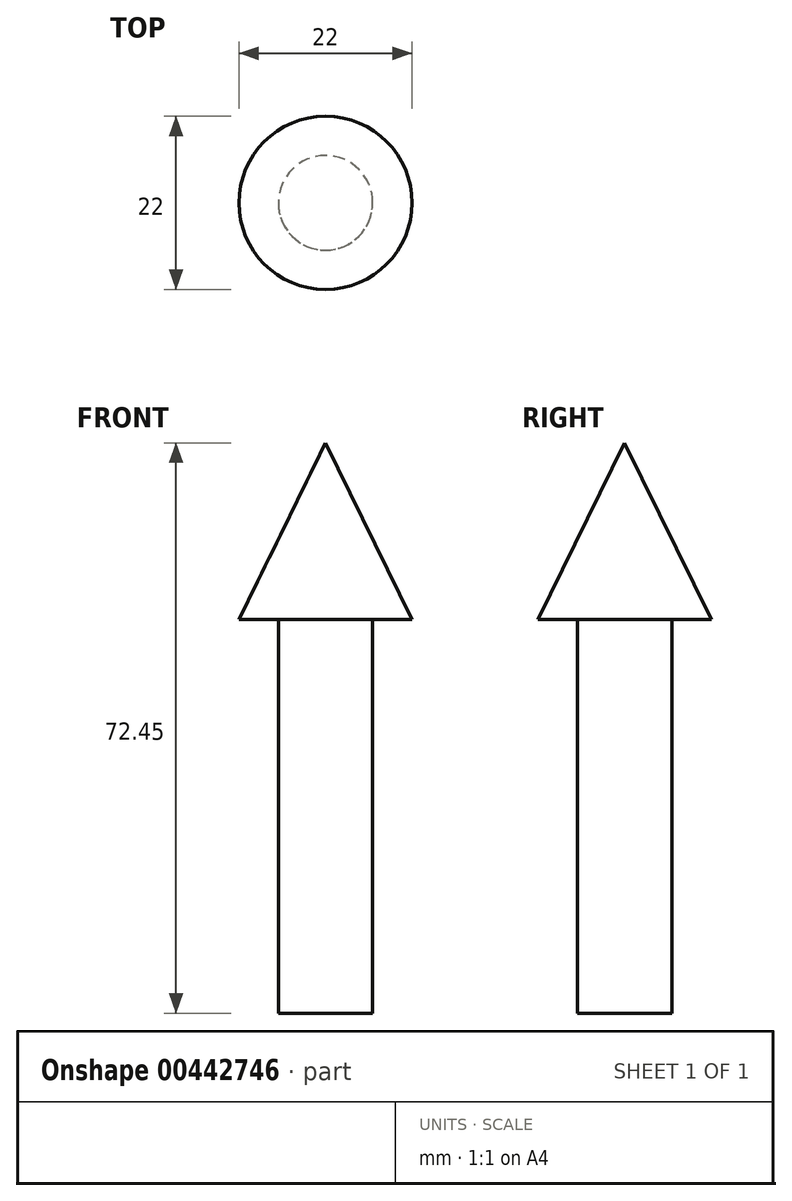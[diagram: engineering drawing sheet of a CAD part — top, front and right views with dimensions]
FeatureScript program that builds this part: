
annotation { "Feature Type Name" : "Feature", "Feature Type Description" : "" }
export const myFeature = defineFeature(function(context is Context, id is Id, definition is map)
    precondition{}
    {
        {
            var Q0;
            Q0=qCreatedBy(makeId("Front.planeOp"),FACE);
            var sketch = newSketch(context, id + "F0", { "sketchPlane" : qUnion([Q0])});
            skLineSegment(sketch, "E0", {"start": v(-30.7, 0) * mm, "end": v(-30.7, 50) * mm});
            skLineSegment(sketch, "E1", {"start": v(-30.7, 50) * mm, "end": v(-18.7, 50) * mm});
            skLineSegment(sketch, "E2", {"start": v(-18.7, 50) * mm, "end": v(-18.7, 0) * mm});
            skLineSegment(sketch, "E3", {"start": v(-18.7, 0) * mm, "end": v(-30.7, 0) * mm});
            skLineSegment(sketch, "E4", {"start": v(-30.7, 50) * mm, "end": v(-35.7, 50) * mm});
            skLineSegment(sketch, "E5", {"start": v(-35.7, 50) * mm, "end": v(-24.7, 72.45) * mm});
            skLineSegment(sketch, "E6", {"start": v(-24.7, 72.45) * mm, "end": v(-13.7, 50) * mm});
            skLineSegment(sketch, "E7", {"start": v(-13.7, 50) * mm, "end": v(-18.7, 50) * mm});
            skLineSegment(sketch, "E8", {"start": v(-24.7, 72.45) * mm, "end": v(-24.7, 50) * mm});
            skLineSegment(sketch, "E9", {"start": v(-24.7, 50) * mm, "end": v(-35.7, 50) * mm});
            skLineSegment(sketch, "E10", {"start": v(-24.7, 0) * mm, "end": v(-24.7, 50) * mm});
            skSolve(sketch);
        }
        {
            var Q0;
            {var subQ0=sQuery(id+"F0.wireOp",EDGE,"E0");Q0=makeQuery(id+"F0.imprint","IMPRINT",FACE,{"disambiguationData":[TD([[makeQuery(id+"F0.imprint","IMPRINT",EDGE,{"derivedFrom":subQ0}),-1.0]])]});}
            var Q1;
            Q1=sQuery(id+"F0.wireOp",EDGE,"E10");
            revolve(context, id + "F1", {"entities" : qUnion([Q0]), "axis" : qUnion([Q1]), "revolveType" : RevolveType.FULL});
        }
        {
            var Q0;
            {var subQ0=sQuery(id+"F0.wireOp",EDGE,"E5");Q0=makeQuery(id+"F0.imprint","IMPRINT",FACE,{"disambiguationData":[TD([[makeQuery(id+"F0.imprint","IMPRINT",EDGE,{"derivedFrom":subQ0}),-1.0]])]});}
            var Q1;
            Q1=sQuery(id+"F0.wireOp",EDGE,"E8");
            revolve(context, id + "F2", {"operationType" : NewBodyOperationType.ADD, "entities" : qUnion([Q0]), "axis" : qUnion([Q1]), "revolveType" : RevolveType.FULL});
        }
    });
